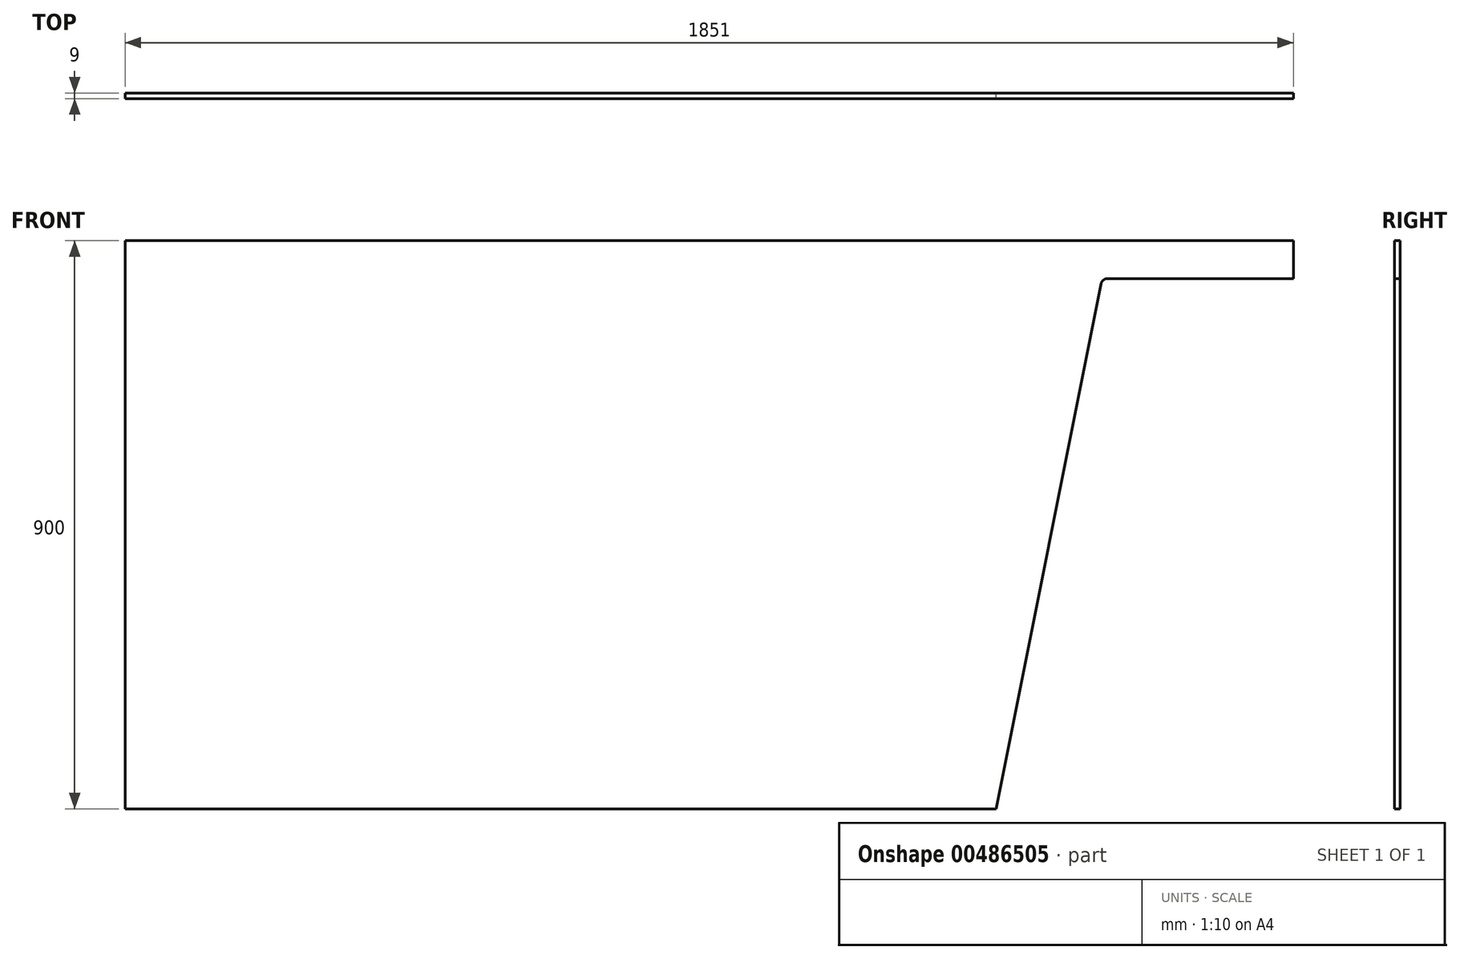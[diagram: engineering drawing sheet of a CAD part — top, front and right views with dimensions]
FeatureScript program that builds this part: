
annotation { "Feature Type Name" : "Feature", "Feature Type Description" : "" }
export const myFeature = defineFeature(function(context is Context, id is Id, definition is map)
    precondition{}
    {
        {
            var Q0;
            Q0=qCreatedBy(makeId("Front.planeOp"),FACE);
            var sketch = newSketch(context, id + "F0", { "sketchPlane" : qUnion([Q0])});
            skLineSegment(sketch, "E0", {"start": v(0, 900) * mm, "end": v(1851, 900) * mm});
            skLineSegment(sketch, "E1", {"start": v(1851, 900) * mm, "end": v(1851, 840) * mm});
            skLineSegment(sketch, "E2", {"start": v(1851, 840) * mm, "end": v(1556.2, 840) * mm});
            skLineSegment(sketch, "E3", {"start": v(1546.4, 831.96) * mm, "end": v(1380, 0) * mm});
            skLineSegment(sketch, "E4", {"start": v(1380, 0) * mm, "end": v(0, 0) * mm});
            skLineSegment(sketch, "E5", {"start": v(0, 900) * mm, "end": v(0, 0) * mm});
            skPoint(sketch, "E6.visualSharp", {"position": v(1548, 840) * mm});
            skArc(sketch, "E6.filletArc", {"start": v(1556.2, 840) * mm, "mid": v(1549.86, 837.73) * mm, "end": v(1546.4, 831.96) * mm});
            skSolve(sketch);
        }
        {
            var Q0;
            Q0=makeQuery(id+"F0.imprint","IMPRINT",FACE,{"disambiguationData":[TD([[makeQuery(id+"F0.imprint","IMPRINT",EDGE,{"derivedFrom":sQuery(id+"F0.wireOp",EDGE,"E0")}),-1.0]])]});
            extrude(context, id + "F1", {"entities" : qUnion([Q0]), "depth" : 9 * mm, "offsetDistance" : 25 * mm});
        }
    });
